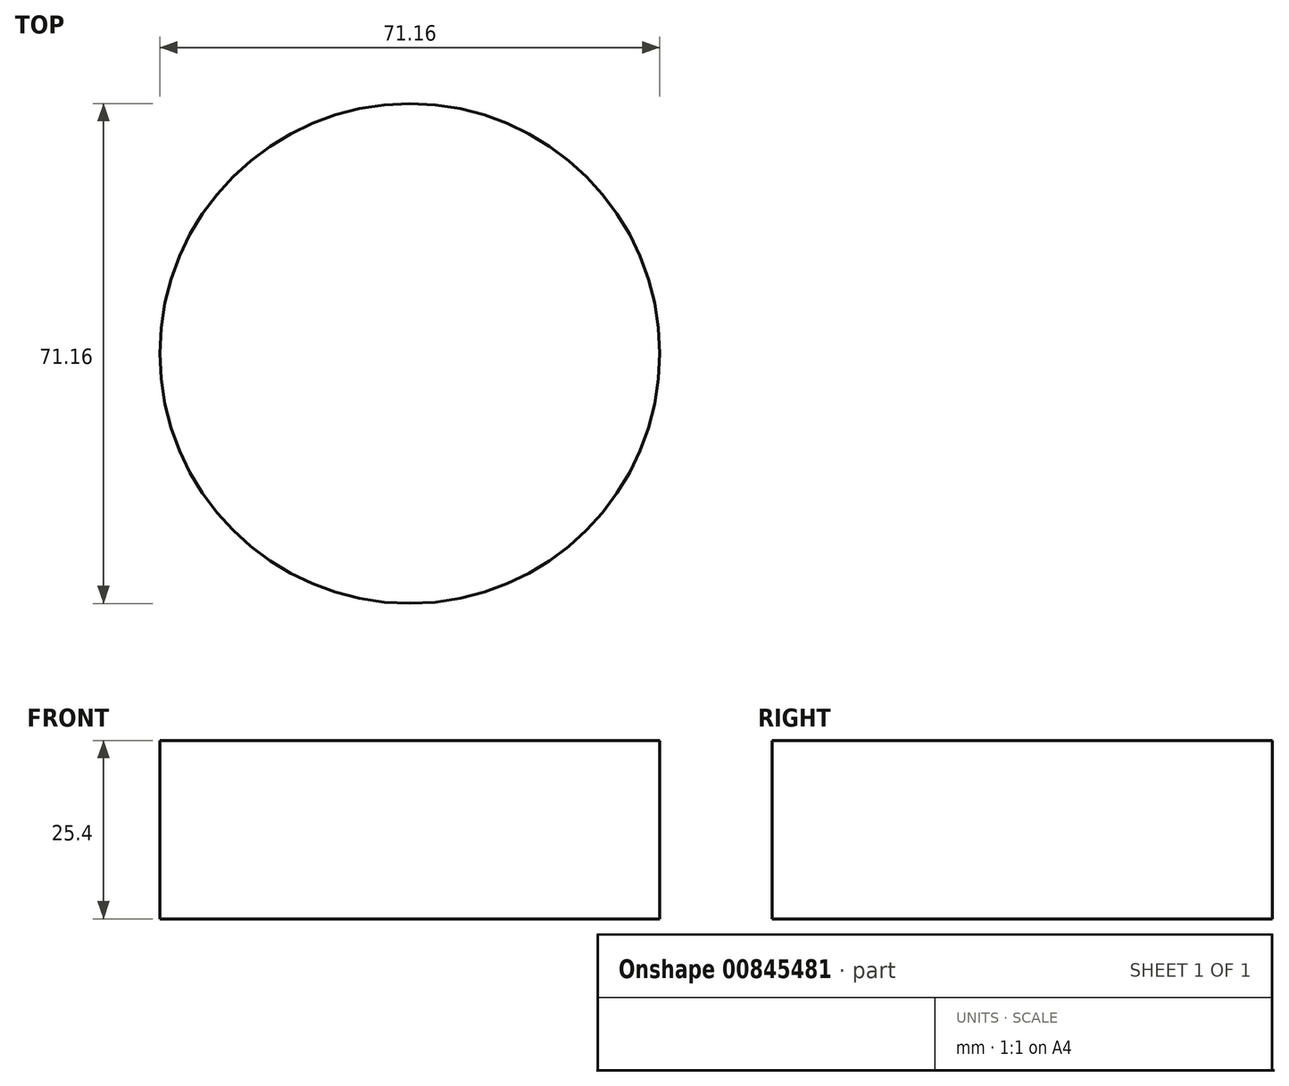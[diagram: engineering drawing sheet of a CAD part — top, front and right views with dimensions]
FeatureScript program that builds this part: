
annotation { "Feature Type Name" : "Feature", "Feature Type Description" : "" }
export const myFeature = defineFeature(function(context is Context, id is Id, definition is map)
    precondition{}
    {
        {
            var Q0;
            Q0=qCreatedBy(makeId("Top.planeOp"),FACE);
            var sketch = newSketch(context, id + "F0", { "sketchPlane" : qUnion([Q0])});
            skCircle(sketch, "E0", {"center": v(0, 0) * mm, "radius": 35.58 * mm});
            skSolve(sketch);
        }
        {
            var Q0;
            Q0=makeQuery(id+"F0.imprint","IMPRINT",FACE,{"disambiguationData":[TD([[makeQuery(id+"F0.imprint","IMPRINT",EDGE,{"derivedFrom":sQuery(id+"F0.wireOp",EDGE,"E0")}),1.0]])]});
            extrude(context, id + "F1", {"entities" : qUnion([Q0]), "depth" : 25.4 * mm, "offsetDistance" : 25.4 * mm});
        }
    });
